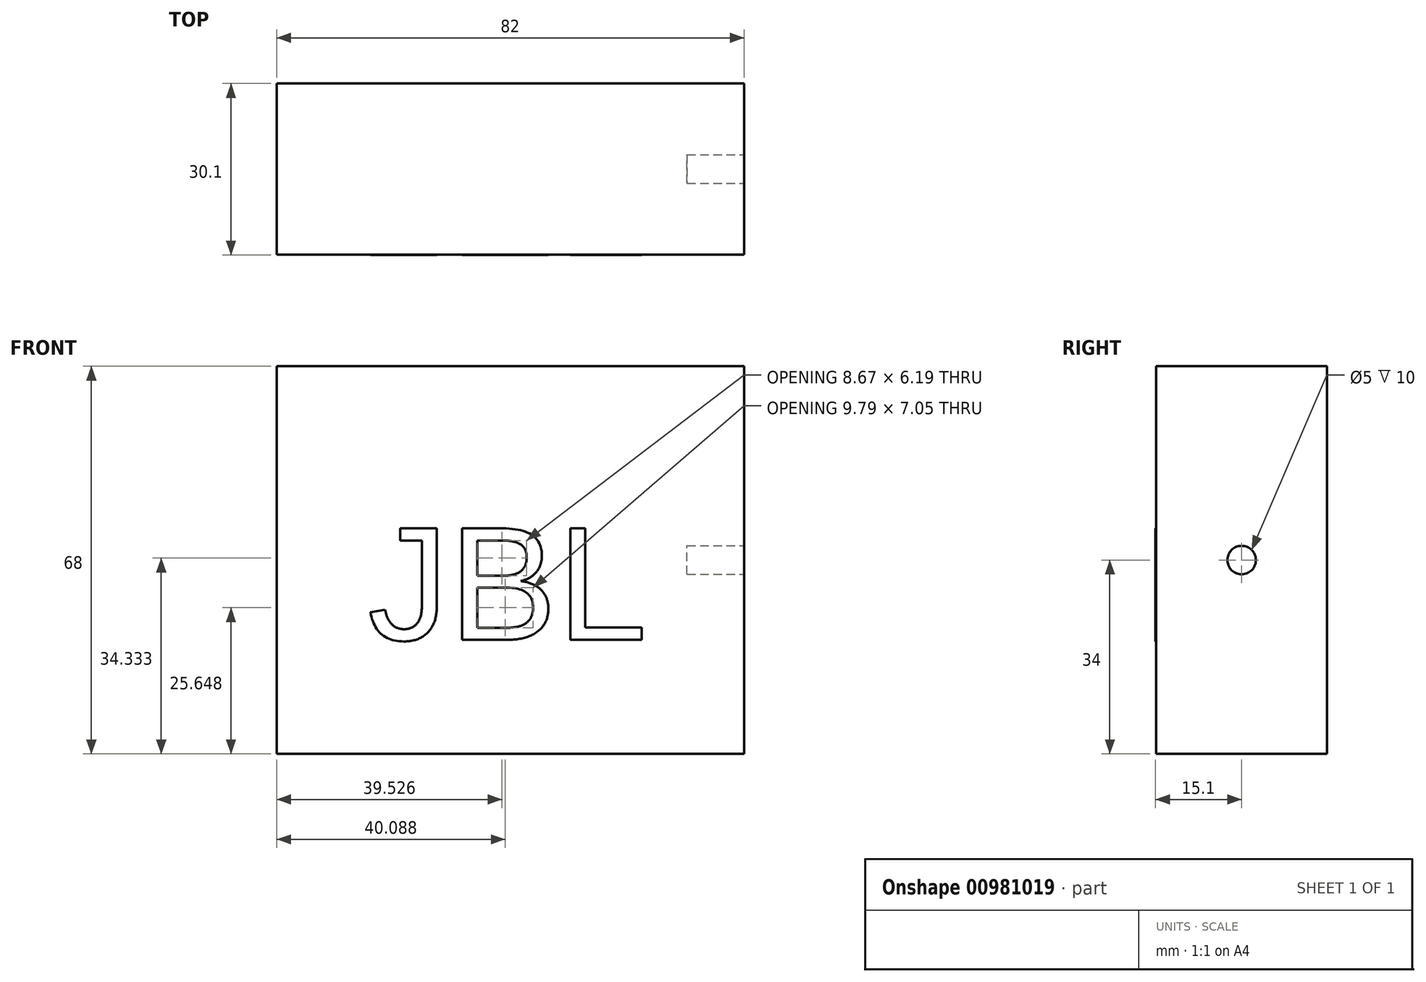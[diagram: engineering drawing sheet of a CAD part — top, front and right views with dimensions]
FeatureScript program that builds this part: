
annotation { "Feature Type Name" : "Feature", "Feature Type Description" : "" }
export const myFeature = defineFeature(function(context is Context, id is Id, definition is map)
    precondition{}
    {
        {
            var Q0;
            Q0=qCreatedBy(makeId("Front.planeOp"),FACE);
            var sketch = newSketch(context, id + "F0", { "sketchPlane" : qUnion([Q0])});
            skLineSegment(sketch, "E0.bottom", {"start": v(-41, 72) * mm, "end": v(41, 72) * mm});
            skLineSegment(sketch, "E0.top", {"start": v(-41, 4) * mm, "end": v(41, 4) * mm});
            skLineSegment(sketch, "E0.left", {"start": v(-41, 72) * mm, "end": v(-41, 4) * mm});
            skLineSegment(sketch, "E0.right", {"start": v(41, 72) * mm, "end": v(41, 4) * mm});
            skSolve(sketch);
        }
        {
            var Q0;
            Q0=makeQuery(id+"F0.imprint","IMPRINT",FACE,{"disambiguationData":[TD([[makeQuery(id+"F0.imprint","IMPRINT",EDGE,{"derivedFrom":sQuery(id+"F0.wireOp",EDGE,"E0.bottom")}),-1.0]])]});
            extrude(context, id + "F1", {"entities" : qUnion([Q0]), "depth" : 30 * mm, "offsetDistance" : 25 * mm});
        }
        {
            var Q0;
            Q0=makeQuery(id+"F1.opExtrude","CAP_FACE",FACE,{"disambiguationData":[OSD([sQuery(id+"F0.wireOp",EDGE,"E0.bottom"),sQuery(id+"F0.wireOp",EDGE,"E0.top"),sQuery(id+"F0.wireOp",EDGE,"E0.left"),sQuery(id+"F0.wireOp",EDGE,"E0.right")])],"isStart":false});
            var sketch = newSketch(context, id + "F2", { "sketchPlane" : qUnion([Q0])});
            skText(sketch, "E1", { "text": "JBL\n", "fontName": "Arimo-Regular.ttf"});
            const initialGuessF2  = {"E1": [-0.025, 0.024, 1, 0, 0.02046]};
            skSetInitialGuess(sketch, initialGuessF2);
            skSolve(sketch);
        }
        {
            var Q0;
            Q0 = qSketchRegion(id + "F2", true);
            extrude(context, id + "F3", {"entities" : qUnion([Q0]), "depth" : 0.1 * mm, "offsetDistance" : 25 * mm});
        }
        {
            var Q0;
            Q0=makeQuery(id+"F1.opExtrude","SWEPT_FACE",FACE,{"disambiguationData":[OSD([sQuery(id+"F0.wireOp",EDGE,"E0.right")])]});
            var sketch = newSketch(context, id + "F4", { "sketchPlane" : qUnion([Q0])});
            skCircle(sketch, "E2", {"center": v(-15, 38) * mm, "radius": 2.5 * mm});
            skLineSegment(sketch, "E3", {"start": v(-15, 72) * mm, "end": v(-15, 4) * mm});
            skLineSegment(sketch, "E4", {"start": v(-30, 38) * mm, "end": v(0, 38) * mm});
            skSolve(sketch);
        }
        {
            var Q0;
            Q0 = qSketchRegion(id + "F4", true);
            extrude(context, id + "F5", {"entities" : qUnion([Q0]), "operationType" : NewBodyOperationType.REMOVE, "oppositeDirection" : true, "depth" : 10 * mm, "offsetDistance" : 25 * mm});
        }
    });
